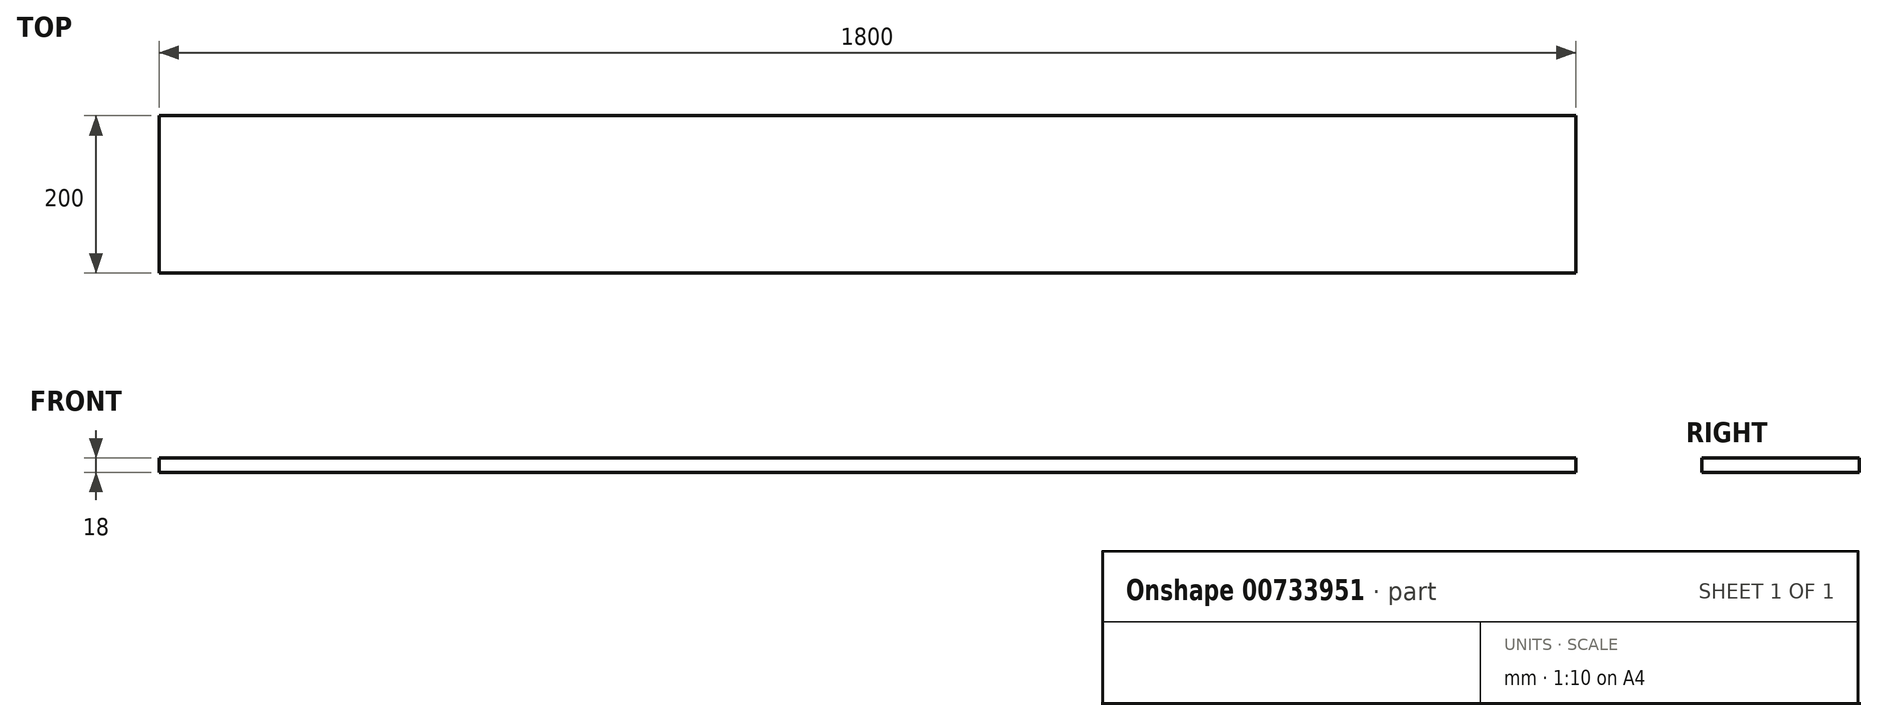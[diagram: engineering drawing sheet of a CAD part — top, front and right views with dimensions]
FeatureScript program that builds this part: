
annotation { "Feature Type Name" : "Feature", "Feature Type Description" : "" }
export const myFeature = defineFeature(function(context is Context, id is Id, definition is map)
    precondition{}
    {
        {
            var Q0;
            Q0=qCreatedBy(makeId("Right.planeOp"),FACE);
            var sketch = newSketch(context, id + "F0", { "sketchPlane" : qUnion([Q0])});
            skLineSegment(sketch, "E0.bottom", {"start": v(0, 0) * mm, "end": v(200, 0) * mm});
            skLineSegment(sketch, "E0.top", {"start": v(0, 18) * mm, "end": v(200, 18) * mm});
            skLineSegment(sketch, "E0.left", {"start": v(0, 0) * mm, "end": v(0, 18) * mm});
            skLineSegment(sketch, "E0.right", {"start": v(200, 0) * mm, "end": v(200, 18) * mm});
            skSolve(sketch);
        }
        {
            var Q0;
            Q0 = qSketchRegion(id + "F0", true);
            extrude(context, id + "F1", {"entities" : qUnion([Q0]), "depth" : 1800 * mm, "offsetDistance" : 25 * mm});
        }
    });
